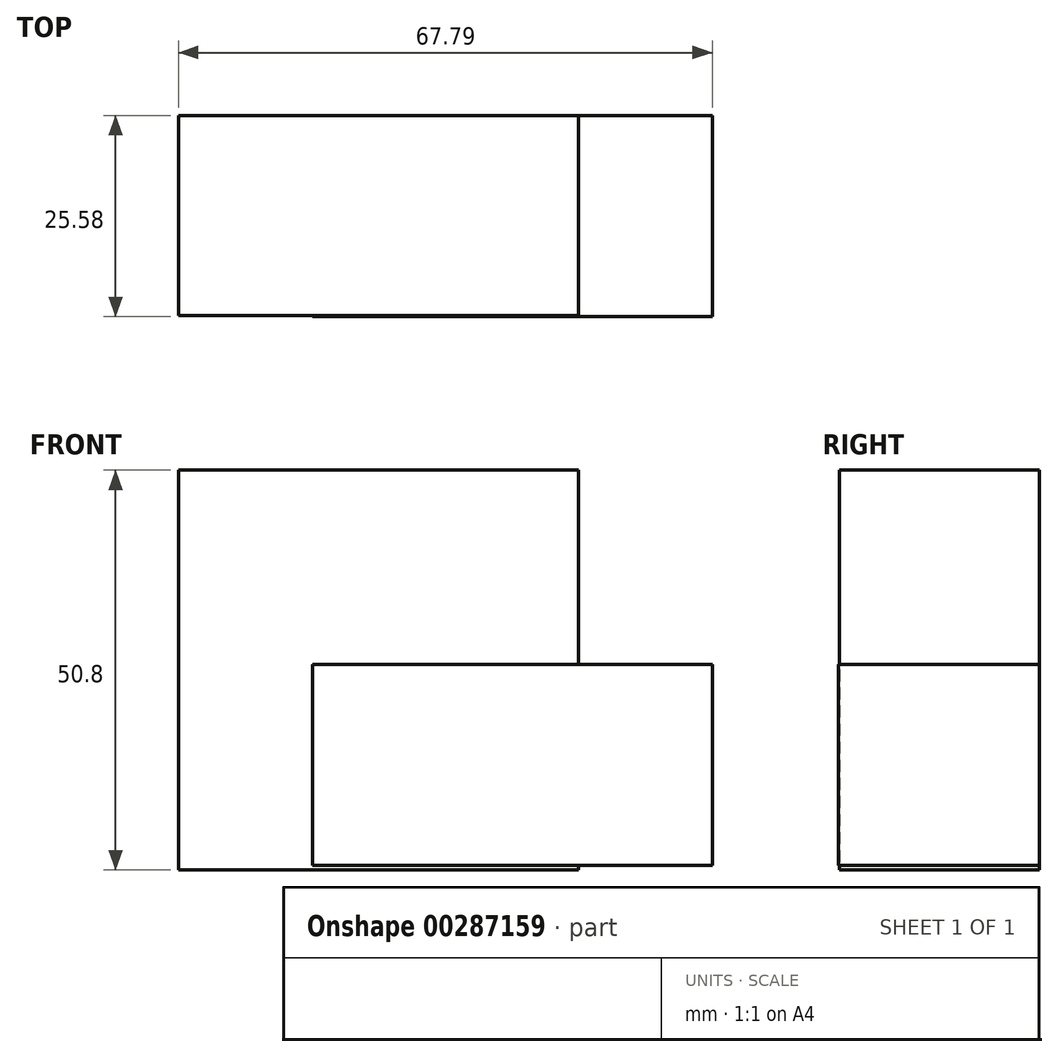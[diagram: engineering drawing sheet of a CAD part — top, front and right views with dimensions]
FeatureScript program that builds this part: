
annotation { "Feature Type Name" : "Feature", "Feature Type Description" : "" }
export const myFeature = defineFeature(function(context is Context, id is Id, definition is map)
    precondition{}
    {
        {
            var Q0;
            Q0=qCreatedBy(makeId("Front.planeOp"),FACE);
            var sketch = newSketch(context, id + "F0", { "sketchPlane" : qUnion([Q0])});
            skLineSegment(sketch, "E0.bottom", {"start": v(-17, 37.43) * mm, "end": v(33.8, 37.43) * mm});
            skLineSegment(sketch, "E0.top", {"start": v(-17, -13.37) * mm, "end": v(33.8, -13.37) * mm});
            skLineSegment(sketch, "E0.left", {"start": v(-17, 37.43) * mm, "end": v(-17, -13.37) * mm});
            skLineSegment(sketch, "E0.right", {"start": v(33.8, 37.43) * mm, "end": v(33.8, -13.37) * mm});
            skSolve(sketch);
        }
        {
            var Q0;
            Q0 = qSketchRegion(id + "F0", true);
            extrude(context, id + "F1", {"entities" : qUnion([Q0]), "depth" : 25.4 * mm});
        }
        {
            var Q0;
            Q0=qCreatedBy(makeId("Right.planeOp"),FACE);
            var sketch = newSketch(context, id + "F2", { "sketchPlane" : qUnion([Q0])});
            skLineSegment(sketch, "E1.bottom", {"start": v(0, 12.78) * mm, "end": v(-25.58, 12.78) * mm});
            skLineSegment(sketch, "E1.top", {"start": v(0, -12.8) * mm, "end": v(-25.58, -12.8) * mm});
            skLineSegment(sketch, "E1.left", {"start": v(0, 12.78) * mm, "end": v(0, -12.8) * mm});
            skLineSegment(sketch, "E1.right", {"start": v(-25.58, 12.78) * mm, "end": v(-25.58, -12.8) * mm});
            skSolve(sketch);
        }
        {
            var Q0;
            Q0 = qSketchRegion(id + "F2", true);
            extrude(context, id + "F3", {"entities" : qUnion([Q0]), "operationType" : NewBodyOperationType.ADD, "depth" : 50.8 * mm});
        }
    });
